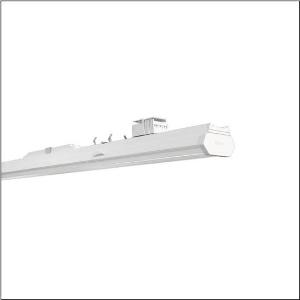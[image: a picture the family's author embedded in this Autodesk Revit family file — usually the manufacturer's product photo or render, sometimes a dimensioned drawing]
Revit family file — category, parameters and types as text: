
# Revit family: licross_r__11_protected_ho_51td11dn4f5s_b27d
name_source: partatom
category: Lighting Fixtures
units: mm (PartAtom-declared; Revit-internal decimal feet)

## family parameters
Cut with Voids When Loaded = No
Host = Face
Light Source = No
Part Type = Normal
Room Calculation Point = No
Round Connector Dimension = Use Diameter
Shared = No

## types (1)
- --- (1 x LED, 15510 lm, 87.3 W, 4000K)
    Apparent Load = 87 VA
    CIE Flux Codes = 84 94 98 99 100
    Color Rendering = 80
    Color Temperature = 4000K
    Default Elevation = 1800 mm
    Description = Licross® 11 Protected HO, luminaire insert, of sheet steel, galvanised, coil coated, white, length: 1.500mm, width: 90mm, height: 101mm, LED rated luminous flux: 15.510lm, light colour: 840, control gear: DALI 2, with plug, 5-pole, with phase selection, mains connection: 220..240V, AC, 50/60Hz, rated input power: 87W, halogen-free wiring, primary light control with lens, of plastic, primary optical cover: cover, of PMMA, light emission: direct distribution, primary light characteristic: symmetric, protection rating (complete): IP54, insulation class (complete): insulation class I (protective earthing), certification: CE, ENEC, VDE, UKCA, protection symbol: D if used in an environment with non-conductive dust loads with corresponding accessories, impact resistance: IK06, permissible ambient temperature for indoor applications: -25..+30°C, corresponds to IFS (International Featured Standards) requirements for safety and quality in the food industry, reducing of maximum allowable ambient temperature of 5°C with ceiling mounting, LABS conformity tested according to VDMA 24364:2018-05, packaging unit: 1 piece
    Height = 92 mm
    Lamp = 1 x LED
    Lamp Light Flux = 15510 lm
    Lamp Power = 87.3 W
    Lamp count = 1
    Length = 1500 mm
    Luminous efficacy = 178 lm/W
    Manufacturer = Siteco
    ModVariant = No
    Model = 51TD11DN4F5S
    Mounting Place = Ceiling
    Mounting Type = Pendant
    Number of Poles = 1
    OnlyDefault = Yes
    Power Factor = 1
    Product Name = Licross® 11 Protected HO
    Product group = luminaire insert
    ProductGroupID = 901
    Protection Class = Protection class I
    Protection Degree = IP 54
    RLX_Detail_Level = 1
    RLX_Emergency_Light_Flux = 0 lm
    RLX_Emergency_Type = 0
    RLX_Emergency_Type_DB = No
    RlxData = <blob elided: 24289 chars, md5=994906dd>
    Socket = socket
    Standby Power = 0 W
    System Light Flux = 15510 lm
    System Power = 87 W
    Type Comments = factory setting: luminous flux: 100 % | dim-lin: 254 | 589 mA
    Type Image = l_1256145.jpg
    URL = http://relux.com
    VarID = @adj_049341
    Voltage = 0 V
    Weight = 0.00 kg
    Width = 88 mm

## geometry (parser evidence)
native form markers: Blend x4, Sweep x11
no freeform markers — native parametric forms only
